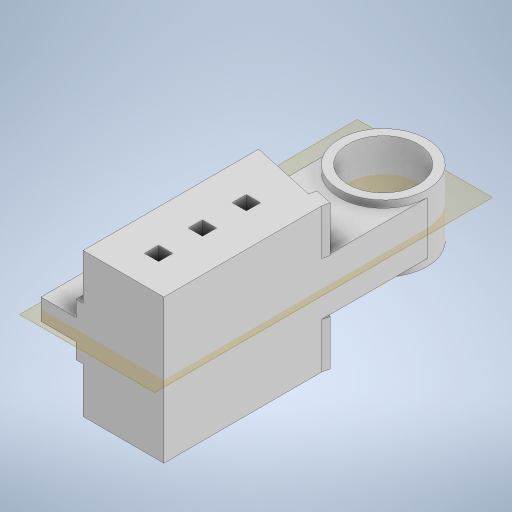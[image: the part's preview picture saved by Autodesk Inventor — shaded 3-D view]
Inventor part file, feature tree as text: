
AUTODESK INVENTOR PART (.ipt)
format: ipt  version: 2023 (Build 270158000, 158)  size: 377,344 bytes
history: native  units: mm
features: sketch x15, extrude x9, mirror x2, plane x1
ambient origin geometry x8: Origin, YZ Plane, XZ Plane, XY Plane, X Axis, Y Axis, Z Axis, Center Point
bodies: Solid1 (feature_tree)
feature tree (27):
  extrude  "Extrusion1"  Depth=25.0mm
  extrude  "Extrusion2"  Depth=15.0mm TaperAngle=0.0deg
  sketch  "Sketch3"  dims[d5=50.0mm d8=3.0mm]
  extrude  "Extrusion3"  Depth=3.0mm
  sketch  "Sketch5"  dims[d11=10.0mm d12=0.0mm d13=25.0mm d14=0.0mm]
  extrude  "Extrusion6"  Depth=50.0mm
  extrude  "Extrusion7"  Depth=25.0mm TaperAngle=0.0deg
  sketch  "Sketch10"  dims[d44=4.0mm d45=13.0mm]
  extrude  "Extrusion8"  Depth=4.0mm
  plane  "Work Plane1"
  mirror  "Mirror1"
  mirror  "Mirror2"
  sketch  "Sketch12"  dims[d48=10.0mm d49=0.0mm]
  sketch  "Sketch13"  dims[d50=30.0mm]
  sketch  "Sketch14"  dims[d51=2.0mm]
  extrude  "Extrusion9"  Depth=4.0mm
  extrude  "Extrusion10"  Depth=13.0mm
  extrude  "Extrusion11"  Depth=4.0mm
  sketch  "Sketch1"  dims[d0=20.0mm d1=25.0mm]
  sketch  "Sketch2"  dims[d2=50.0mm d3=15.0mm d4=0.0mm]
  sketch  "Sketch4"  dims[d9=6.0mm d10=50.0mm]
  sketch  "Sketch8"  dims[d40=4.0mm d41=4.0mm]
  sketch  "Sketch9"  dims[d42=13.0mm d43=4.0mm]
  sketch  "Sketch11"  dims[d46=4.0mm d47=4.0mm]
  sketch  "Sketch15"  dims[d52=13.0mm d53=0.0mm]
  sketch  "Sketch16"  dims[d54=11.5mm]
  sketch  "Sketch17"  dims[d55=4.0mm d56=4.0mm d57=12.5mm d58=4.0mm d59=4.0mm d60=12.5mm d61=4.0mm d62=4.0mm d63=50.0mm d64=0.0mm d65=7.5mm d66=5.0mm d67=2.0mm d68=0.0mm d69=25.0mm d70=2.0mm d71=0.0mm d72=2.0mm d73=0.0mm d36=0.5mm d37=0.872665mm d38=0.5mm d39=0.872665mm]
